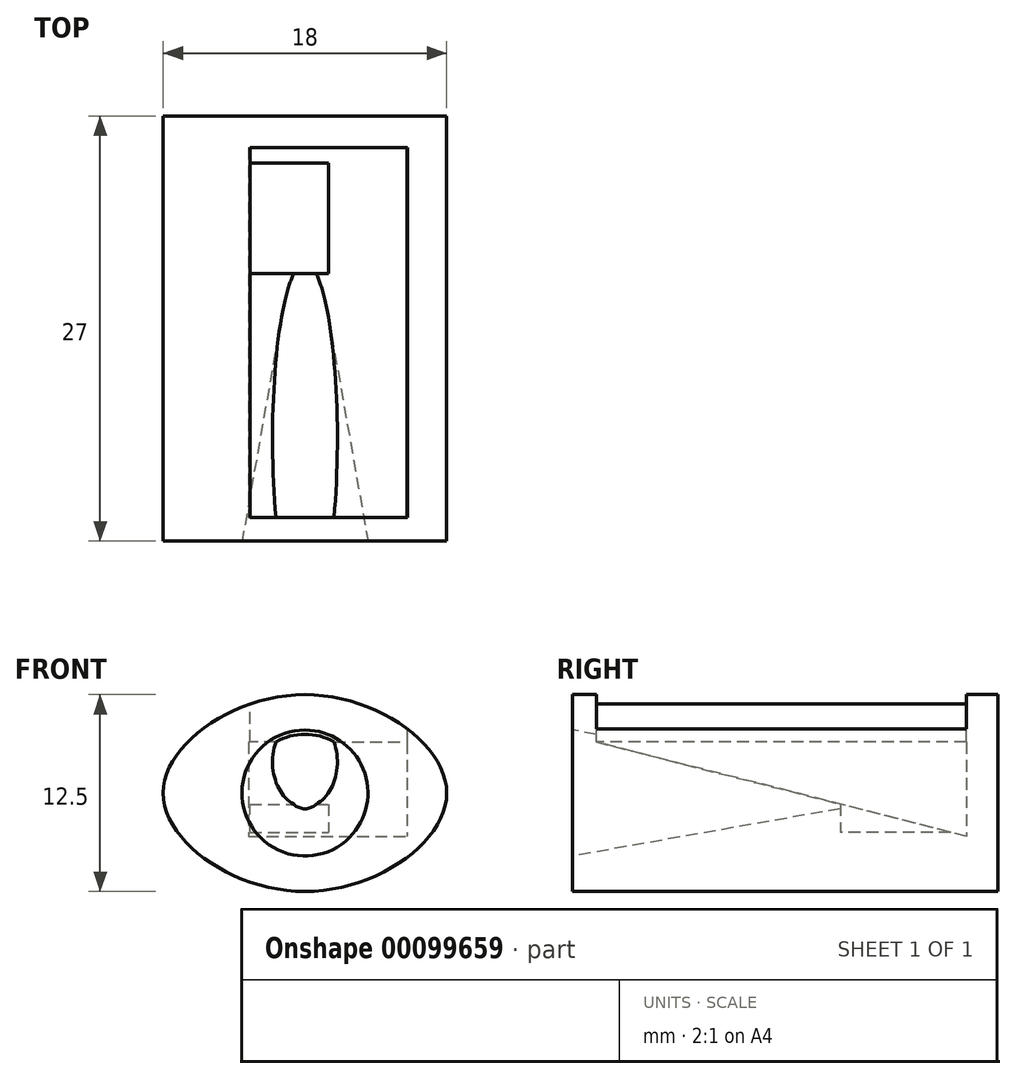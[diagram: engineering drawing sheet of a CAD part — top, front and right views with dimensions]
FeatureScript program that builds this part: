
annotation { "Feature Type Name" : "Feature", "Feature Type Description" : "" }
export const myFeature = defineFeature(function(context is Context, id is Id, definition is map)
    precondition{}
    {
        {
            var Q0;
            Q0=qCreatedBy(makeId("Front.planeOp"),FACE);
            var sketch = newSketch(context, id + "F0", { "sketchPlane" : qUnion([Q0])});
            skLineSegment(sketch, "E0.bottom", {"start": v(9, -6.25) * mm, "end": v(-9, -6.25) * mm});
            skLineSegment(sketch, "E0.top", {"start": v(9, 6.25) * mm, "end": v(-9, 6.25) * mm});
            skLineSegment(sketch, "E0.left", {"start": v(9, -6.25) * mm, "end": v(9, 6.25) * mm});
            skLineSegment(sketch, "E0.right", {"start": v(-9, -6.25) * mm, "end": v(-9, 6.25) * mm});
            skPoint(sketch, "E0.middle", {"position": v(0, 0) * mm});
            skFitSpline(sketch, "E1", {"points": [v(9, 0) * mm, v(0, 6.25) * mm, v(-9, 0) * mm, v(0, -6.25) * mm, v(9, 0) * mm]});
            skSolve(sketch);
        }
        {
            var Q0;
            {var subQ0=sQuery(id+"F0.wireOp",EDGE,"E1");var subQ1=makeQuery(id+"F0.imprint","INTERSECT",VERTEX,{"derivedFrom":[sQuery(id+"F0.wireOp",EDGE,"E0.top"),subQ0]});Q0=makeQuery(id+"F0.imprint","IMPRINT",FACE,{"disambiguationData":[TD([[makeQuery(id+"F0.imprint","IMPRINT",EDGE,{"disambiguationData":[TD([[subQ1,1.0]])],"derivedFrom":subQ0}),1.0]])]});}
            extrude(context, id + "F1", {"entities" : qUnion([Q0]), "depth" : 27 * mm});
        }
        {
            var Q0;
            Q0=qCreatedBy(makeId("Top.planeOp"),FACE);
            cPlane(context, id + "F2", {"entities" : qUnion([Q0]), "cplaneType" : CPlaneType.OFFSET, "offset" : 6.25 * mm, "width" : 150 * mm, "height" : 150 * mm});
        }
        {
            var Q0;
            Q0=qCreatedBy(id+"F2.planeOp",FACE);
            var sketch = newSketch(context, id + "F3", { "sketchPlane" : qUnion([Q0])});
            skLineSegment(sketch, "E2.bottom", {"start": v(6.5, -25.5) * mm, "end": v(-3.5, -25.5) * mm});
            skLineSegment(sketch, "E2.top", {"start": v(6.5, -2) * mm, "end": v(-3.5, -2) * mm});
            skLineSegment(sketch, "E2.left", {"start": v(6.5, -25.5) * mm, "end": v(6.5, -2) * mm});
            skLineSegment(sketch, "E2.right", {"start": v(-3.5, -25.5) * mm, "end": v(-3.5, -2) * mm});
            skPoint(sketch, "E2.middle", {"position": v(1.5, -13.75) * mm});
            skSolve(sketch);
        }
        {
            var Q0;
            Q0 = qSketchRegion(id + "F3", true);
            extrude(context, id + "F4", {"entities" : qUnion([Q0]), "operationType" : NewBodyOperationType.REMOVE, "oppositeDirection" : true, "depth" : 3 * mm});
        }
        {
            var Q0;
            Q0=qCreatedBy(makeId("Right.planeOp"),FACE);
            cPlane(context, id + "F5", {"entities" : qUnion([Q0]), "cplaneType" : CPlaneType.OFFSET, "offset" : 6.25 * mm, "width" : 150 * mm, "height" : 150 * mm});
        }
        {
            var Q0;
            Q0=qCreatedBy(makeId("Right.planeOp"),FACE);
            var sketch = newSketch(context, id + "F6", { "sketchPlane" : qUnion([Q0])});
            skLineSegment(sketch, "E3", {"start": v(-27, 0) * mm, "end": v(-10, 0) * mm});
            skLineSegment(sketch, "E4", {"start": v(-27, 0) * mm, "end": v(-27, 4) * mm});
            skLineSegment(sketch, "E5", {"start": v(-10, 0) * mm, "end": v(-10, 1) * mm});
            skLineSegment(sketch, "E6", {"start": v(-10, 1) * mm, "end": v(-27, 4) * mm});
            skSolve(sketch);
        }
        {
            var Q0;
            Q0 = qSketchRegion(id + "F6", true);
            var Q1;
            Q1=sQuery(id+"F6.wireOp",EDGE,"E3");
            revolve(context, id + "F7", {"operationType" : NewBodyOperationType.REMOVE, "entities" : qUnion([Q0]), "axis" : qUnion([Q1]), "revolveType" : RevolveType.FULL, "oppositeDirection" : true});
        }
        {
            var Q0;
            Q0=qCreatedBy(makeId("Top.planeOp"),FACE);
            cPlane(context, id + "F8", {"entities" : qUnion([Q0]), "cplaneType" : CPlaneType.OFFSET, "offset" : 2.5 * mm, "oppositeDirection" : true, "width" : 150 * mm, "height" : 150 * mm});
        }
        {
            var Q0;
            Q0=qCreatedBy(id+"F8.planeOp",FACE);
            var sketch = newSketch(context, id + "F9", { "sketchPlane" : qUnion([Q0])});
            skLineSegment(sketch, "E7", {"start": v(-3.5, -10) * mm, "end": v(1.5, -10) * mm});
            skLineSegment(sketch, "E8", {"start": v(1.5, -10) * mm, "end": v(1.5, -2) * mm});
            skLineSegment(sketch, "E9", {"start": v(1.5, -2) * mm, "end": v(-3.5, -2) * mm});
            skLineSegment(sketch, "E10", {"start": v(-3.5, -2) * mm, "end": v(-3.5, -10) * mm});
            skSolve(sketch);
        }
        {
            var Q0;
            Q0 = qSketchRegion(id + "F9", true);
            extrude(context, id + "F10", {"entities" : qUnion([Q0]), "operationType" : NewBodyOperationType.REMOVE, "depth" : 4 * mm});
        }
        {
            var Q0;
            Q0 = qSketchRegion(id + "F9", true);
            extrude(context, id + "F11", {"entities" : qUnion([Q0]), "operationType" : NewBodyOperationType.REMOVE, "depth" : 4 * mm});
        }
        {
            var Q0;
            Q0=qCreatedBy(id+"F5.planeOp",FACE);
            var sketch = newSketch(context, id + "F12", { "sketchPlane" : qUnion([Q0])});
            skLineSegment(sketch, "E11", {"start": v(-2, 3.25) * mm, "end": v(-25.5, 3.25) * mm});
            skLineSegment(sketch, "E12", {"start": v(-2, 3.25) * mm, "end": v(-2, -2.75) * mm});
            skLineSegment(sketch, "E13", {"start": v(-2, -2.75) * mm, "end": v(-25.5, 3.25) * mm});
            skSolve(sketch);
        }
        {
            var Q0;
            Q0 = qSketchRegion(id + "F12", true);
            extrude(context, id + "F13", {"entities" : qUnion([Q0]), "operationType" : NewBodyOperationType.REMOVE, "oppositeDirection" : true, "depth" : 9.83 * mm, "hasSecondDirection" : true, "secondDirectionOppositeDirection" : false, "secondDirectionDepth" : 0.22 * mm});
        }
    });
